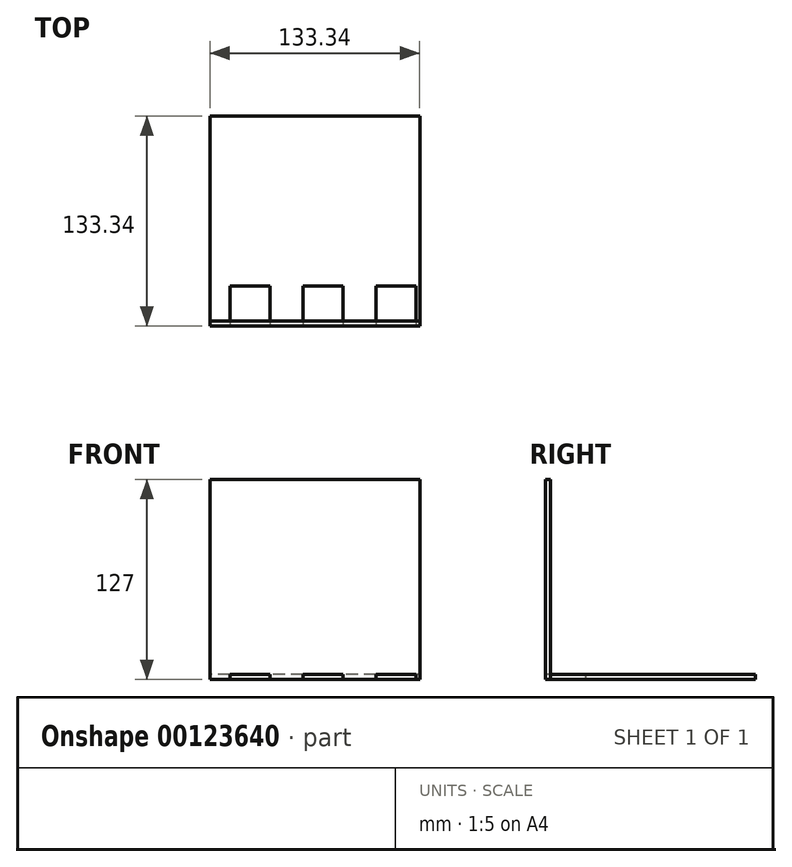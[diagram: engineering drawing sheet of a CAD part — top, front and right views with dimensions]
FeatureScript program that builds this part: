
annotation { "Feature Type Name" : "Feature", "Feature Type Description" : "" }
export const myFeature = defineFeature(function(context is Context, id is Id, definition is map)
    precondition{}
    {
        {
            var Q0;
            Q0=qCreatedBy(makeId("Top.planeOp"),FACE);
            var sketch = newSketch(context, id + "F0", { "sketchPlane" : qUnion([Q0])});
            skLineSegment(sketch, "E0.bottom", {"start": v(-66.67, 66.68) * mm, "end": v(66.68, 66.68) * mm});
            skLineSegment(sketch, "E0.top", {"start": v(-66.68, -66.67) * mm, "end": v(66.67, -66.67) * mm});
            skLineSegment(sketch, "E0.left", {"start": v(-66.67, 66.68) * mm, "end": v(-66.68, -66.67) * mm});
            skLineSegment(sketch, "E0.right", {"start": v(66.68, 66.68) * mm, "end": v(66.67, -66.67) * mm});
            skPoint(sketch, "E0.middle", {"position": v(0, 0) * mm});
            skSolve(sketch);
        }
        {
            var Q0;
            Q0 = qSketchRegion(id + "F0", true);
            extrude(context, id + "F1", {"entities" : qUnion([Q0]), "depth" : 3.17 * mm});
        }
        {
            var Q0;
            Q0=qCreatedBy(makeId("Top.planeOp"),FACE);
            var sketch = newSketch(context, id + "F2", { "sketchPlane" : qUnion([Q0])});
            skLineSegment(sketch, "E1.bottom", {"start": v(-66.68, -63.5) * mm, "end": v(66.67, -63.5) * mm});
            skLineSegment(sketch, "E1.top", {"start": v(-66.68, -66.67) * mm, "end": v(66.67, -66.67) * mm});
            skLineSegment(sketch, "E1.left", {"start": v(-66.68, -63.5) * mm, "end": v(-66.68, -66.67) * mm});
            skLineSegment(sketch, "E1.right", {"start": v(66.67, -63.5) * mm, "end": v(66.67, -66.67) * mm});
            skSolve(sketch);
        }
        {
            var Q0;
            Q0 = qSketchRegion(id + "F2", true);
            extrude(context, id + "F3", {"entities" : qUnion([Q0]), "depth" : 127 * mm});
        }
        {
            var Q0;
            Q0=makeQuery(id+"F1.opExtrude","SWEPT_FACE",FACE,{"disambiguationData":[OSD([sQuery(id+"F0.wireOp",EDGE,"E0.top")])]});
            var sketch = newSketch(context, id + "F4", { "sketchPlane" : qUnion([Q0])});
            skLineSegment(sketch, "E2.bottom", {"start": v(-53.86, 3.18) * mm, "end": v(-28.46, 3.18) * mm});
            skLineSegment(sketch, "E2.top", {"start": v(-53.86, 0) * mm, "end": v(-28.46, 0) * mm});
            skLineSegment(sketch, "E2.left", {"start": v(-53.86, 3.18) * mm, "end": v(-53.86, 0) * mm});
            skLineSegment(sketch, "E2.right", {"start": v(-28.46, 3.18) * mm, "end": v(-28.46, 0) * mm});
            skLineSegment(sketch, "E3.bottom", {"start": v(-7.5, 3.18) * mm, "end": v(17.9, 3.18) * mm});
            skLineSegment(sketch, "E3.top", {"start": v(-7.5, 0) * mm, "end": v(17.9, 0) * mm});
            skLineSegment(sketch, "E3.left", {"start": v(-7.5, 3.18) * mm, "end": v(-7.5, 0) * mm});
            skLineSegment(sketch, "E3.right", {"start": v(17.9, 3.18) * mm, "end": v(17.9, 0) * mm});
            skLineSegment(sketch, "E4.bottom", {"start": v(38.85, 3.18) * mm, "end": v(64.25, 3.18) * mm});
            skLineSegment(sketch, "E4.top", {"start": v(38.85, 0) * mm, "end": v(64.25, 0) * mm});
            skLineSegment(sketch, "E4.left", {"start": v(38.85, 3.18) * mm, "end": v(38.85, 0) * mm});
            skLineSegment(sketch, "E4.right", {"start": v(64.25, 3.18) * mm, "end": v(64.25, 0) * mm});
            skSolve(sketch);
        }
        {
            var Q0;
            Q0=makeQuery(id+"F4.imprint","IMPRINT",FACE,{"disambiguationData":[TD([[makeQuery(id+"F4.imprint","IMPRINT",EDGE,{"derivedFrom":sQuery(id+"F4.wireOp",EDGE,"E2.bottom")}),-1.0]])]});
            var Q1;
            Q1=makeQuery(id+"F4.imprint","IMPRINT",FACE,{"disambiguationData":[TD([[makeQuery(id+"F4.imprint","IMPRINT",EDGE,{"derivedFrom":sQuery(id+"F4.wireOp",EDGE,"E3.bottom")}),-1.0]])]});
            var Q2;
            Q2=makeQuery(id+"F4.imprint","IMPRINT",FACE,{"disambiguationData":[TD([[makeQuery(id+"F4.imprint","IMPRINT",EDGE,{"derivedFrom":sQuery(id+"F4.wireOp",EDGE,"E4.bottom")}),-1.0]])]});
            extrude(context, id + "F5", {"entities" : qUnion([Q0, Q1, Q2]), "operationType" : NewBodyOperationType.REMOVE, "oppositeDirection" : true, "depth" : 25.4 * mm});
        }
        {
            var Q0;
            Q0=makeQuery(id+"F3.opExtrude","SWEPT_BODY",BODY,{"disambiguationData":[OSD([sQuery(id+"F2.wireOp",EDGE,"E1.bottom"),sQuery(id+"F2.wireOp",EDGE,"E1.top"),sQuery(id+"F2.wireOp",EDGE,"E1.left"),sQuery(id+"F2.wireOp",EDGE,"E1.right")])]});
            var Q1;
            Q1=makeQuery(id+"F1.opExtrude","SWEPT_BODY",BODY,{"disambiguationData":[OSD([sQuery(id+"F0.wireOp",EDGE,"E0.bottom"),sQuery(id+"F0.wireOp",EDGE,"E0.top"),sQuery(id+"F0.wireOp",EDGE,"E0.left"),sQuery(id+"F0.wireOp",EDGE,"E0.right")])]});
            booleanBodies(context, id + "F6", {"operationType" : BooleanOperationType.SUBTRACTION, "tools" : qUnion([Q0]), "targets" : qUnion([Q1]), "keepTools" : true});
        }
    });
